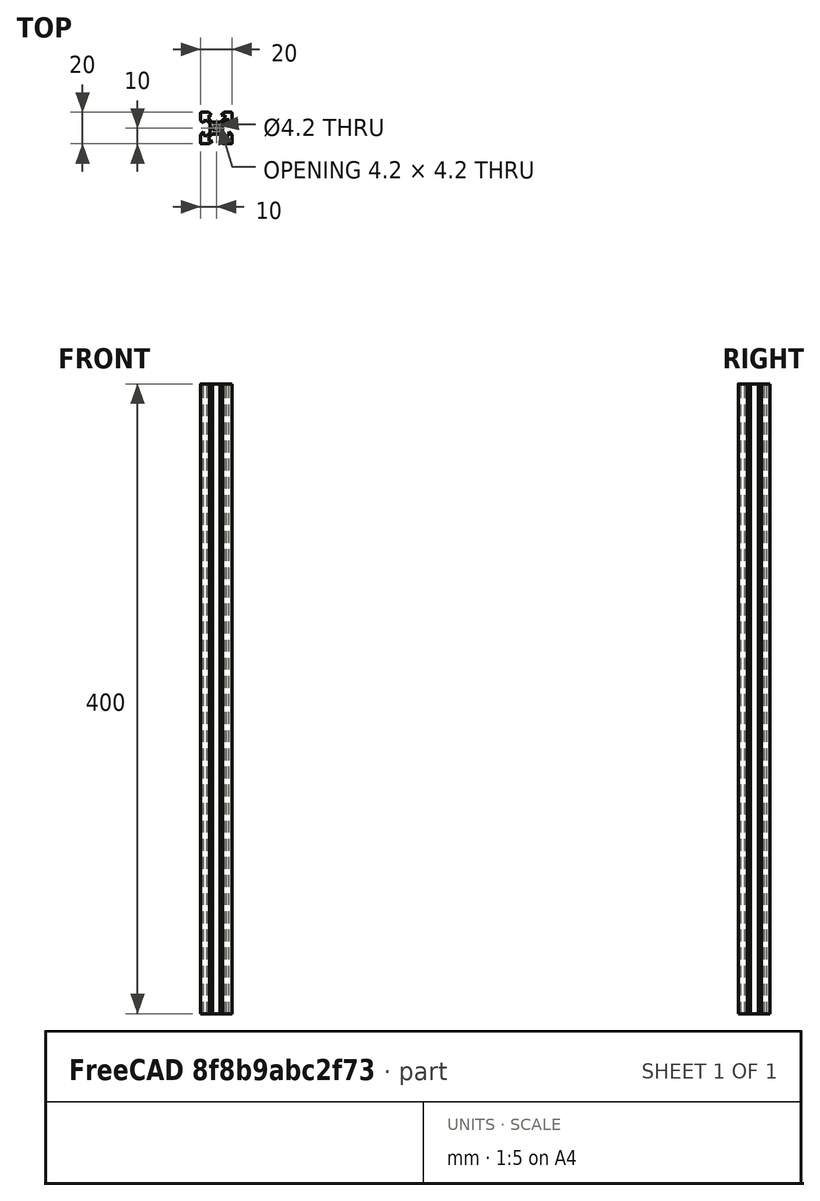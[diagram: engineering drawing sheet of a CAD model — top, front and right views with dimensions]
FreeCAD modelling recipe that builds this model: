
FCSTD DOCUMENT  (FreeCAD 1.1R20260325 (Git shallow))
Label: 20x20 aluminum profile V-slot
License: All rights reserved
LicenseURL: https://en.wikipedia.org/wiki/All_rights_reserved
objects: Sketcher::SketchObject×1, PartDesign::Pad×1, PartDesign::Body×1, App::Point×1
note: 6 computed .brp shape members not serialized (recipe doc carries the construction recipe); baked Part::Feature solids carry a one-line shape summary decoded from their .brp

FEATURE [Sketcher::SketchObject] Sketch
  ArcFitTolerance = 1e-06
  AttachmentSupport = -> [XY_Plane]
  ExternalTypes = [0]
  FullyConstrained = true
  MakeInternals = false
  MapMode = 5
  _ExternalGeoVersion = 0
  sketch-geometry (56):
    g0: ArcOfCircle CenterX=0 CenterY=0 CenterZ=0 NormalX=0 NormalY=0 NormalZ=1 AngleXU=0 Radius=2.1 StartAngle=0 EndAngle=1.5708
    g1: LineSegment StartX=3.9 StartY=0 StartZ=0 EndX=3.9 EndY=2.83934 EndZ=0
    g2: LineSegment StartX=2.83934 StartY=3.9 StartZ=0 EndX=0 EndY=3.9 EndZ=0
    g3: LineSegment StartX=3.9 StartY=2.83934 StartZ=0 EndX=6.56066 EndY=5.5 EndZ=0
    g4: LineSegment StartX=2.83934 StartY=3.9 StartZ=0 EndX=5.5 EndY=6.56066 EndZ=0
    g5: LineSegment StartX=5.5 StartY=6.56066 StartZ=0 EndX=5.5 EndY=8.2 EndZ=0
    g6: LineSegment StartX=5.5 StartY=8.2 StartZ=0 EndX=3.1 EndY=8.2 EndZ=0
    g7: LineSegment StartX=3.1 StartY=8.2 StartZ=0 EndX=4.9 EndY=10 EndZ=0
    g8: LineSegment StartX=4.9 StartY=10 StartZ=0 EndX=9.5 EndY=10 EndZ=0
    g9: LineSegment StartX=6.56066 StartY=5.5 StartZ=0 EndX=8.2 EndY=5.5 EndZ=0
    g10: LineSegment StartX=8.2 StartY=5.5 StartZ=0 EndX=8.2 EndY=3.1 EndZ=0
    g11: LineSegment StartX=8.2 StartY=3.1 StartZ=0 EndX=10 EndY=4.9 EndZ=0
    g12: LineSegment StartX=10 StartY=4.9 StartZ=0 EndX=10 EndY=9.5 EndZ=0
    g13: ArcOfCircle CenterX=9.5 CenterY=9.5 CenterZ=0 NormalX=0 NormalY=0 NormalZ=1 AngleXU=0 Radius=0.5 StartAngle=-9e-16 EndAngle=1.5708
    g14: ArcOfCircle CenterX=0 CenterY=0 CenterZ=0 NormalX=0 NormalY=0 NormalZ=1 AngleXU=0 Radius=2.1 StartAngle=1.5708 EndAngle=3.14159
    g15: LineSegment StartX=-3.9 StartY=4e-16 StartZ=0 EndX=-3.9 EndY=2.83934 EndZ=0
    g16: LineSegment StartX=-2.83934 StartY=3.9 StartZ=0 EndX=0 EndY=3.9 EndZ=0
    g17: LineSegment StartX=-3.9 StartY=2.83934 StartZ=0 EndX=-5.8 EndY=4.73934 EndZ=0
    g18: LineSegment StartX=-2.83934 StartY=3.9 StartZ=0 EndX=-4.73934 EndY=5.8 EndZ=0
    g19: LineSegment StartX=-4.73934 StartY=5.8 StartZ=0 EndX=-4.73934 EndY=8.2 EndZ=0
    g20: LineSegment StartX=-4.73934 StartY=8.2 StartZ=0 EndX=-3.1 EndY=8.2 EndZ=0
    g21: LineSegment StartX=-3.1 StartY=8.2 StartZ=0 EndX=-4.9 EndY=10 EndZ=0
    g22: LineSegment StartX=-4.9 StartY=10 StartZ=0 EndX=-9.5 EndY=10 EndZ=0
    g23: LineSegment StartX=-5.8 StartY=4.73934 StartZ=0 EndX=-8.2 EndY=4.73934 EndZ=0
    g24: LineSegment StartX=-8.2 StartY=4.73934 StartZ=0 EndX=-8.2 EndY=3.1 EndZ=0
    g25: LineSegment StartX=-8.2 StartY=3.1 StartZ=0 EndX=-10 EndY=4.9 EndZ=0
    g26: LineSegment StartX=-10 StartY=4.9 StartZ=0 EndX=-10 EndY=9.5 EndZ=0
    g27: ArcOfCircle CenterX=-9.5 CenterY=9.5 CenterZ=0 NormalX=0 NormalY=0 NormalZ=1 AngleXU=0 Radius=0.5 StartAngle=1.5708 EndAngle=3.14159
    g28: ArcOfCircle CenterX=0 CenterY=0 CenterZ=0 NormalX=0 NormalY=0 NormalZ=1 AngleXU=0 Radius=2.1 StartAngle=4.71239 EndAngle=6.28319
    g29: LineSegment StartX=3.9 StartY=0 StartZ=0 EndX=3.9 EndY=-2.83934 EndZ=0
    g30: LineSegment StartX=2.83934 StartY=-3.9 StartZ=0 EndX=0 EndY=-3.9 EndZ=0
    g31: LineSegment StartX=3.9 StartY=-2.83934 StartZ=0 EndX=5.8 EndY=-4.73934 EndZ=0
    g32: LineSegment StartX=2.83934 StartY=-3.9 StartZ=0 EndX=4.73934 EndY=-5.8 EndZ=0
    g33: LineSegment StartX=4.73934 StartY=-5.8 StartZ=0 EndX=4.73934 EndY=-8.2 EndZ=0
    g34: LineSegment StartX=4.73934 StartY=-8.2 StartZ=0 EndX=2.33934 EndY=-8.2 EndZ=0
    g35: LineSegment StartX=2.33934 StartY=-8.2 StartZ=0 EndX=4.13934 EndY=-10 EndZ=0
    g36: LineSegment StartX=4.13934 StartY=-10 StartZ=0 EndX=9.5 EndY=-10 EndZ=0
    g37: LineSegment StartX=5.8 StartY=-4.73934 StartZ=0 EndX=8.2 EndY=-4.73934 EndZ=0
    g38: LineSegment StartX=8.2 StartY=-4.73934 StartZ=0 EndX=8.2 EndY=-2.33934 EndZ=0
    g39: LineSegment StartX=8.2 StartY=-2.33934 StartZ=0 EndX=10 EndY=-4.13934 EndZ=0
    g40: LineSegment StartX=10 StartY=-4.13934 StartZ=0 EndX=10 EndY=-9.5 EndZ=0
    g41: ArcOfCircle CenterX=9.5 CenterY=-9.5 CenterZ=0 NormalX=0 NormalY=0 NormalZ=1 AngleXU=0 Radius=0.5 StartAngle=4.71239 EndAngle=6.28319
    g42: ArcOfCircle CenterX=-1e-16 CenterY=0 CenterZ=0 NormalX=0 NormalY=0 NormalZ=1 AngleXU=0 Radius=2.1 StartAngle=3.14159 EndAngle=4.71239
    g43: LineSegment StartX=-3.9 StartY=4e-16 StartZ=0 EndX=-3.9 EndY=-2.83934 EndZ=0
    g44: LineSegment StartX=-2.83934 StartY=-3.9 StartZ=0 EndX=0 EndY=-3.9 EndZ=0
    g45: LineSegment StartX=-3.9 StartY=-2.83934 StartZ=0 EndX=-5.8 EndY=-4.73934 EndZ=0
    g46: LineSegment StartX=-2.83934 StartY=-3.9 StartZ=0 EndX=-4.73934 EndY=-5.8 EndZ=0
    g47: LineSegment StartX=-4.73934 StartY=-5.8 StartZ=0 EndX=-4.73934 EndY=-8.2 EndZ=0
    g48: LineSegment StartX=-4.73934 StartY=-8.2 StartZ=0 EndX=-2.33934 EndY=-8.2 EndZ=0
    g49: LineSegment StartX=-2.33934 StartY=-8.2 StartZ=0 EndX=-4.13934 EndY=-10 EndZ=0
    g50: LineSegment StartX=-4.13934 StartY=-10 StartZ=0 EndX=-9.5 EndY=-10 EndZ=0
    g51: LineSegment StartX=-5.8 StartY=-4.73934 StartZ=0 EndX=-8.2 EndY=-4.73934 EndZ=0
    g52: LineSegment StartX=-8.2 StartY=-4.73934 StartZ=0 EndX=-8.2 EndY=-2.33934 EndZ=0
    g53: LineSegment StartX=-8.2 StartY=-2.33934 StartZ=0 EndX=-10 EndY=-4.13934 EndZ=0
    g54: LineSegment StartX=-10 StartY=-4.13934 StartZ=0 EndX=-10 EndY=-9.5 EndZ=0
    g55: ArcOfCircle CenterX=-9.5 CenterY=-9.5 CenterZ=0 NormalX=0 NormalY=0 NormalZ=1 AngleXU=0 Radius=0.5 StartAngle=3.14159 EndAngle=4.71239
  constraints (159):
    c: Coincident(g0,g-1)
    c: PointOnObject(g0,g-2)
    c: PointOnObject(g0,g-1)
    c: Vertical(g1)
    c: Horizontal(g2)
    c: PointOnObject(g1,g-1)
    c: PointOnObject(g2,g-2)
    c: Vertical(g5)
    c: Horizontal(g6)
    c: Coincident(g7,g6)
    c: Coincident(g8,g7)
    c: Horizontal(g8)
    c: Coincident(g3,g9)
    c: Horizontal(g9)
    c: Coincident(g9,g10)
    c: Vertical(g10)
    c: Coincident(g10,g11)
    c: Coincident(g11,g12)
    c: Vertical(g12)
    c: Tangent(g12,g13) = -1.5708
    c: Tangent(g8,g13) = 1.5708
    c: Coincident(g1,g3)
    c: Coincident(g2,g4)
    c: Parallel(g3,g4)
    c: Coincident(g5,g6)
    c: Coincident(g5,g4)
    c: Equal(g3,g4)
    c: Equal(g11,g7)
    c: Equal(g12,g8)
    c: Equal(g6,g10)
    c: Equal(g1,g2)
    c: Distance(g10,g1) = 4.3
    c: Distance(g4,g3) = 1.5
    c: Distance(g-2,g5) = 5.5
    c: DistanceX(g10,g11) = 1.8
    c: Distance(g6,g-2) = 3.1
    c: Radius(g13) = 0.5
    c: Distance(g2,g6) = 4.3
    c: Distance(g-2,g12) = 10
    c: Distance(g-1,g8) = 10
    c: Angle(g11,g10) = 0.785398
    c: Distance(g0,g1) = 1.8
    c: Distance(g2,g0) = 1.8
    c: Vertical(g15)
    c: Horizontal(g16)
    c: Vertical(g19)
    c: Horizontal(g20)
    c: Coincident(g21,g20)
    c: Coincident(g22,g21)
    c: Horizontal(g22)
    c: Coincident(g17,g23)
    c: Horizontal(g23)
    c: Coincident(g23,g24)
    c: Vertical(g24)
    c: Coincident(g24,g25)
    c: Coincident(g25,g26)
    c: Vertical(g26)
    c: Tangent(g26,g27) = 1.5708
    c: Tangent(g22,g27) = -1.5708
    c: Coincident(g15,g17)
    c: Coincident(g16,g18)
    c: Parallel(g17,g18)
    c: Coincident(g19,g20)
    c: Coincident(g19,g18)
    c: Equal(g17,g18)
    c: Equal(g25,g21)
    c: Equal(g26,g22)
    c: Equal(g20,g24)
    c: Equal(g15,g16)
    c: Distance(g24,g15) = 4.3
    c: Distance(g18,g17) = 1.5
    c: Radius(g27) = 0.5
    c: Distance(g16,g20) = 4.3
    c: Angle(g25,g24) = -0.785398
    c: Distance(g14,g15) = 1.8
    c: Vertical(g29)
    c: Horizontal(g30)
    c: Vertical(g33)
    c: Horizontal(g34)
    c: Coincident(g35,g34)
    c: Coincident(g36,g35)
    c: Horizontal(g36)
    c: Coincident(g31,g37)
    c: Horizontal(g37)
    c: Coincident(g37,g38)
    c: Coincident(g38,g39)
    c: Coincident(g39,g40)
    c: Tangent(g40,g41) = 1.5708
    c: Tangent(g36,g41) = -1.5708
    c: Coincident(g29,g31)
    c: Coincident(g30,g32)
    c: Parallel(g31,g32)
    c: Coincident(g33,g34)
    c: Coincident(g33,g32)
    c: Equal(g31,g32)
    c: Equal(g39,g35)
    c: Equal(g40,g36)
    c: Equal(g34,g38)
    c: Equal(g29,g30)
    c: Distance(g32,g31) = 1.5
    c: Radius(g41) = 0.5
    c: Distance(g30,g34) = 4.3
    c: Angle(g39,g38) = -0.785398
    c: Distance(g30,g28) = 1.8
    c: Vertical(g43)
    c: Horizontal(g44)
    c: Vertical(g47)
    c: Coincident(g49,g48)
    c: Coincident(g50,g49)
    c: Coincident(g45,g51)
    c: Horizontal(g51)
    c: Coincident(g51,g52)
    c: Coincident(g52,g53)
    c: Coincident(g53,g54)
    c: Tangent(g54,g55) = -1.5708
    c: Tangent(g50,g55) = 1.5708
    c: Coincident(g43,g45)
    c: Coincident(g44,g46)
    c: Parallel(g45,g46)
    c: Coincident(g47,g48)
    c: Coincident(g47,g46)
    c: Equal(g45,g46)
    c: Equal(g53,g49)
    c: Equal(g54,g50)
    c: Equal(g48,g52)
    c: Equal(g43,g44)
    c: Distance(g46,g45) = 1.5
    c: Radius(g55) = 0.5
    c: Angle(g53,g52) = 0.785398
    c: Coincident(g14,g0)
    c: Coincident(g42,g14)
    c: Coincident(g42,g28)
    c: Coincident(g28,g0)
    c: Coincident(g43,g15)
    c: Coincident(g28,g0)
    c: Coincident(g14,g0)
    c: Coincident(g29,g1)
    c: PointOnObject(g28,g-2)
    c: Coincident(g44,g30)
    c: PointOnObject(g30,g-2)
    c: Coincident(g16,g2)
    c: Tangent(g38,g10)
    c: Tangent(g40,g12)
    c: Tangent(g36,g50)
    c: Tangent(g34,g48)
    c: Tangent(g52,g24)
    c: Tangent(g54,g26)
    c: PointOnObject(g14,g-1)
    c: PointOnObject(g42,g-1)
    c: Angle(g21,g20) = 0.785398
    c: Angle(g48,g49) = 0.785398
    c: Angle(g35,g34) = 0.785398
    c: Equal(g10,g38)
    c: Equal(g33,g38)
    c: Equal(g33,g47)
    c: Equal(g47,g51)
    c: Equal(g51,g23)
    c: Equal(g8,g22)
    c: Equal(g50,g36)
FEATURE [PartDesign::Pad] Pad
  Direction = (0,0,1)
  Length = 400
  Length2 = 10
  Profile = -> Sketch
  ReferenceAxis = -> Sketch [N_Axis]
  Refine = true
  SideType = 0
  Suppressed = false
  Type = 0
  Type2 = 0
FEATURE [PartDesign::Body] Body  label="V-slot base"
  AllowCompound = false
  Group = -> [Sketch,Pad]
  Origin = -> Origin
  Tip = -> Pad
FEATURE [App::Point] Origin001  label="Origin"
  Role = Origin
